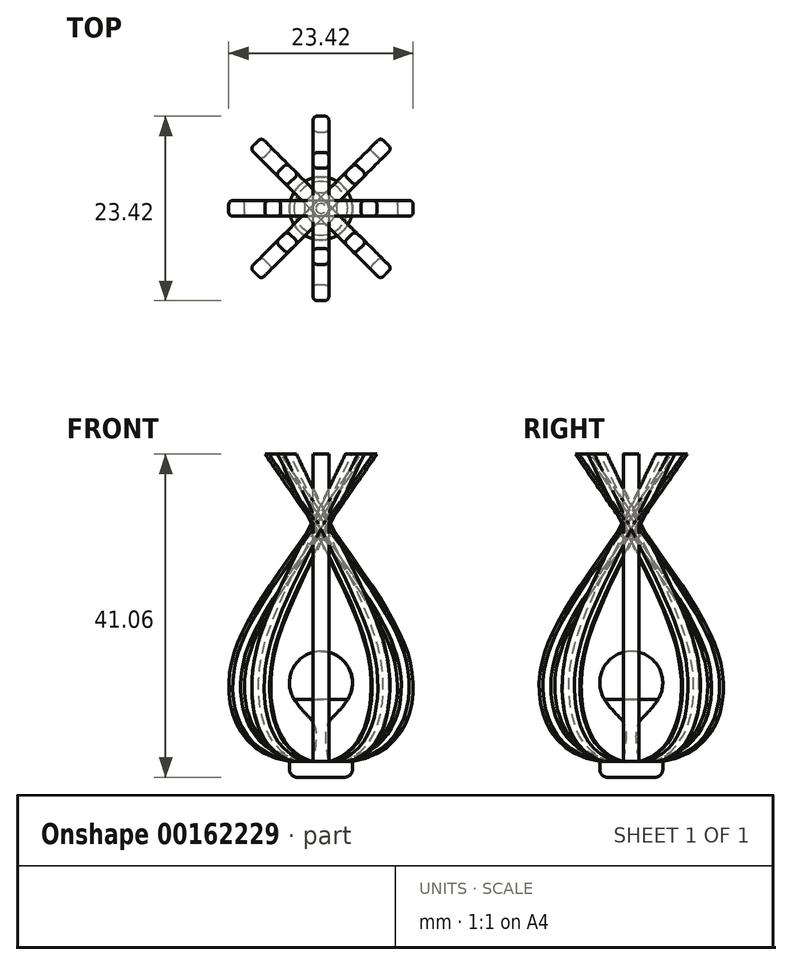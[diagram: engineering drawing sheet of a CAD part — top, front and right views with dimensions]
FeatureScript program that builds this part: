
annotation { "Feature Type Name" : "Feature", "Feature Type Description" : "" }
export const myFeature = defineFeature(function(context is Context, id is Id, definition is map)
    precondition{}
    {
        {
            var Q0;
            Q0=qCreatedBy(makeId("Top.planeOp"),FACE);
            var sketch = newSketch(context, id + "F0", { "sketchPlane" : qUnion([Q0])});
            skLineSegment(sketch, "E0.bottom", {"start": v(-0.5, 4) * mm, "end": v(0.5, 4) * mm});
            skLineSegment(sketch, "E0.top", {"start": v(-0.5, 2) * mm, "end": v(0.5, 2) * mm});
            skLineSegment(sketch, "E0.left", {"start": v(-1, 3.5) * mm, "end": v(-1, 2.5) * mm});
            skLineSegment(sketch, "E0.right", {"start": v(1, 3.5) * mm, "end": v(1, 2.5) * mm});
            skPoint(sketch, "E1.visualSharp", {"position": v(-1, 4) * mm});
            skArc(sketch, "E1.filletArc", {"start": v(-0.5, 4) * mm, "mid": v(-0.85, 3.85) * mm, "end": v(-1, 3.5) * mm});
            skPoint(sketch, "E2.visualSharp", {"position": v(1, 4) * mm});
            skArc(sketch, "E2.filletArc", {"start": v(1, 3.5) * mm, "mid": v(0.85, 3.85) * mm, "end": v(0.5, 4) * mm});
            skPoint(sketch, "E3.visualSharp", {"position": v(1, 2) * mm});
            skArc(sketch, "E3.filletArc", {"start": v(0.5, 2) * mm, "mid": v(0.85, 2.15) * mm, "end": v(1, 2.5) * mm});
            skPoint(sketch, "E4.visualSharp", {"position": v(-1, 2) * mm});
            skArc(sketch, "E4.filletArc", {"start": v(-1, 2.5) * mm, "mid": v(-0.85, 2.15) * mm, "end": v(-0.5, 2) * mm});
            skSolve(sketch);
        }
        {
            var Q0;
            Q0=qCreatedBy(makeId("Right.planeOp"),FACE);
            var sketch = newSketch(context, id + "F1", { "sketchPlane" : qUnion([Q0])});
            skFitSpline(sketch, "E5", {"points": [v(-2, 0) * mm, v(5.7, 10) * mm, v(-11.1, 39.06) * mm], "startDerivative": vector(47.8, 8.02) * mm, "endDerivative": vector(-53.74, 79.28) * mm});
            skLineSegment(sketch, "E6", {"start": v(0, 22.68) * mm, "end": v(0, 72.85) * mm, "construction": true});
            skSolve(sketch);
        }
        {
            var Q0;
            Q0 = qSketchRegion(id + "F0", true);
            var Q1;
            Q1 = qConstructionFilter(qBodyType(qCreatedBy(id + "F1" ,EDGE), BodyType.WIRE), ConstructionObject.NO);
            sweep(context, id + "F2", {"profiles" : qUnion([Q0]), "path" : qUnion([Q1]), "keepProfileOrientation" : true});
        }
        {
            var Q0;
            Q0=makeQuery(id+"F2.opSweep","SWEPT_BODY",BODY,{"disambiguationData":[OSD([sQuery(id+"F0.wireOp",EDGE,"E0.bottom"),sQuery(id+"F0.wireOp",EDGE,"E0.top"),sQuery(id+"F0.wireOp",EDGE,"E0.left"),sQuery(id+"F0.wireOp",EDGE,"E0.right"),sQuery(id+"F0.wireOp",EDGE,"E1.filletArc"),sQuery(id+"F0.wireOp",EDGE,"E2.filletArc"),sQuery(id+"F0.wireOp",EDGE,"E3.filletArc"),sQuery(id+"F0.wireOp",EDGE,"E4.filletArc"),sQuery(id+"F1.wireOp",EDGE,"E5")])]});
            var Q1;
            Q1=sQuery(id+"F1.wireOp",EDGE,"E6");
            circularPattern(context, id + "F3", {"entities" : qUnion([Q0]), "axis" : qUnion([Q1]), "angle" : 360 * degree, "instanceCount" : 8, "equalSpace" : true});
        }
        {
            var Q0;
            Q0=qCreatedBy(makeId("Front.planeOp"),FACE);
            var sketch = newSketch(context, id + "F4", { "sketchPlane" : qUnion([Q0])});
            skArc(sketch, "E7", {"start": v(3.4, 7.9) * mm, "mid": v(3.5, 11.95) * mm, "end": v(0, 14) * mm});
            skLineSegment(sketch, "E8", {"start": v(0, 14) * mm, "end": v(0, 6) * mm});
            skLineSegment(sketch, "E9", {"start": v(0, 6) * mm, "end": v(0, 14) * mm});
            skFitSpline(sketch, "E10", {"points": [v(3.4, 7.9) * mm, v(0.8, 4.56) * mm, v(1, 0) * mm], "startDerivative": vector(-7.88, -12.2) * mm, "endDerivative": vector(1.53, -8.96) * mm});
            skLineSegment(sketch, "E11", {"start": v(1, 0) * mm, "end": v(0, 0) * mm});
            skLineSegment(sketch, "E12", {"start": v(0, 0) * mm, "end": v(0, 6) * mm});
            skSolve(sketch);
        }
        {
            var Q0;
            Q0 = qSketchRegion(id + "F4", true);
            var Q1;
            Q1=sQuery(id+"F4.wireOp",EDGE,"E12");
            revolve(context, id + "F5", {"entities" : qUnion([Q0]), "axis" : qUnion([Q1]), "revolveType" : RevolveType.FULL});
        }
        {
            var Q0;
            Q0=qCreatedBy(makeId("Top.planeOp"),FACE);
            var sketch = newSketch(context, id + "F6", { "sketchPlane" : qUnion([Q0])});
            skCircle(sketch, "E13", {"center": v(0, 0) * mm, "radius": 4 * mm});
            skSolve(sketch);
        }
        {
            var Q0;
            Q0 = qSketchRegion(id + "F6", true);
            extrude(context, id + "F7", {"entities" : qUnion([Q0]), "oppositeDirection" : true, "depth" : 2 * mm});
        }
        {
            var Q0;
            Q0=makeQuery(id+"F7.opExtrude","CAP_EDGE",EDGE,{"disambiguationData":[OSD([sQuery(id+"F6.wireOp",EDGE,"E13")])],"isStart":false});
            fillet(context, id + "F8", {"entities" : qUnion([Q0]), "radius" : 1 * mm, "tangentPropagation" : true, "allowEdgeOverflow" : false});
        }
        {
            var Q0;
            Q0=makeQuery(id+"F3.opPattern","COPY",FACE,{"derivedFrom":makeQuery(id+"F2.opSweep","CAP_FACE",FACE,{"disambiguationData":[OSD([sQuery(id+"F0.wireOp",EDGE,"E0.bottom"),sQuery(id+"F0.wireOp",EDGE,"E0.top"),sQuery(id+"F0.wireOp",EDGE,"E0.left"),sQuery(id+"F0.wireOp",EDGE,"E0.right"),sQuery(id+"F0.wireOp",EDGE,"E1.filletArc"),sQuery(id+"F0.wireOp",EDGE,"E2.filletArc"),sQuery(id+"F0.wireOp",EDGE,"E3.filletArc"),sQuery(id+"F0.wireOp",EDGE,"E4.filletArc"),sQuery(id+"F1.wireOp",VERTEX,"E5.end")])],"isStart":false}),"instanceName":"2"});
            var sketch = newSketch(context, id + "F9", { "sketchPlane" : qUnion([Q0])});
            skCircle(sketch, "E14", {"center": v(0, -1) * mm, "radius": 0.25 * mm});
            skLineSegment(sketch, "E15", {"start": v(-3.32, 0) * mm, "end": v(17.19, 0) * mm, "construction": true});
            skPoint(sketch, "E15.endSnap0", {"position": v(0.82, 0) * mm});
            skSolve(sketch);
        }
        {
            var Q0;
            Q0=sQuery(id+"F9.wireOp",EDGE,"E14");
            var Q1;
            Q1=sQuery(id+"F9.wireOp",EDGE,"E15");
            revolve(context, id + "F10", {"bodyType" : ToolBodyType.SURFACE, "surfaceEntities" : qUnion([Q0]), "axis" : qUnion([Q1]), "revolveType" : RevolveType.ONE_DIRECTION, "oppositeDirection" : true, "angle" : 180 * degree});
        }
    });
